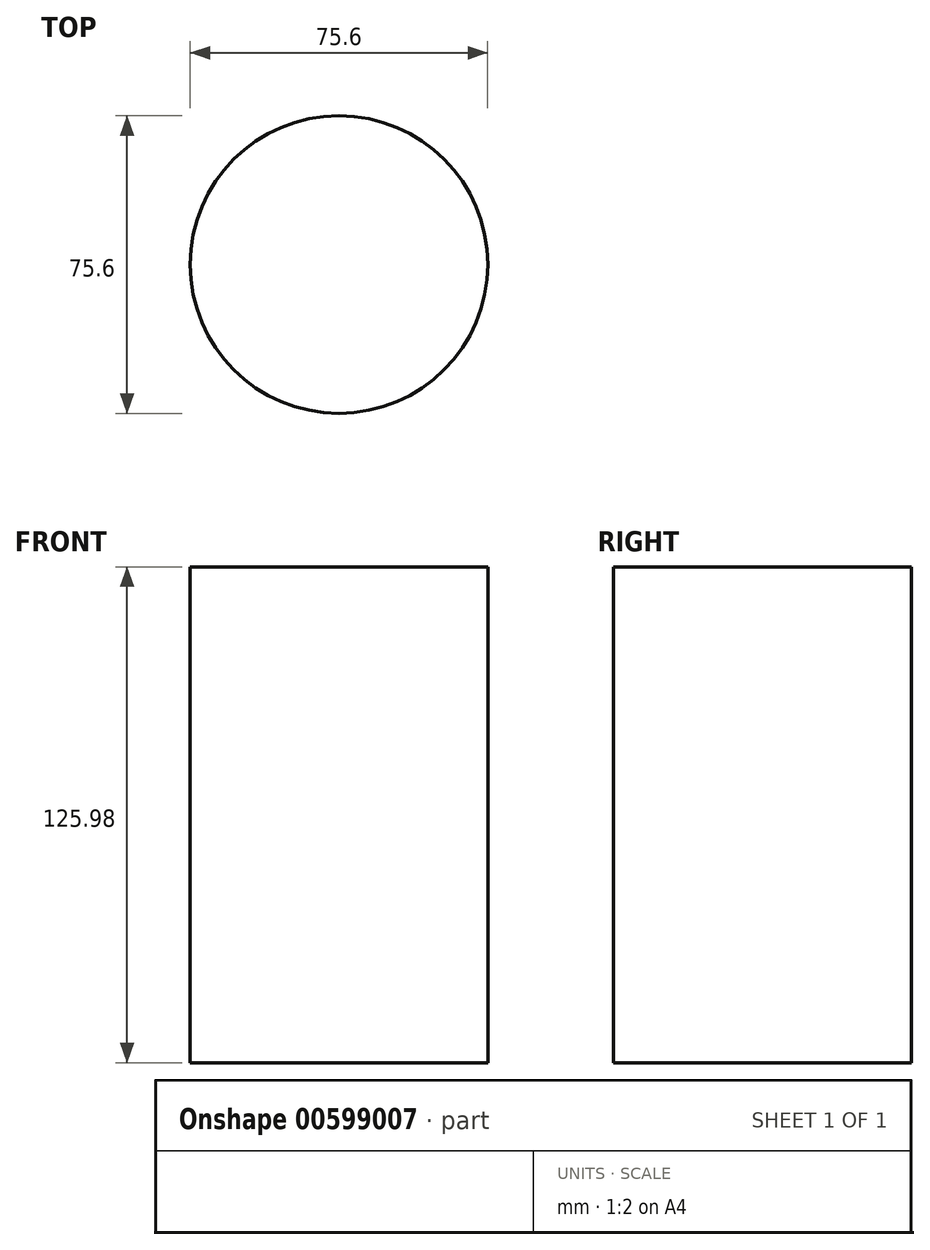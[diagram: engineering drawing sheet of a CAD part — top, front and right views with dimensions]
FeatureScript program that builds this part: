
annotation { "Feature Type Name" : "Feature", "Feature Type Description" : "" }
export const myFeature = defineFeature(function(context is Context, id is Id, definition is map)
    precondition{}
    {
        {
            var Q0;
            Q0=qCreatedBy(makeId("Top.planeOp"),FACE);
            var sketch = newSketch(context, id + "F0", { "sketchPlane" : qUnion([Q0])});
            skCircle(sketch, "E0", {"center": v(-17.9, 8.87) * mm, "radius": 37.8 * mm});
            skSolve(sketch);
        }
        {
            var Q0;
            Q0=makeQuery(id+"F0.imprint","IMPRINT",FACE,{"disambiguationData":[TD([[makeQuery(id+"F0.imprint","IMPRINT",EDGE,{"derivedFrom":sQuery(id+"F0.wireOp",EDGE,"E0")}),1.0]])]});
            extrude(context, id + "F1", {"entities" : qUnion([Q0]), "depth" : 125.98 * mm, "offsetDistance" : 25.4 * mm});
        }
    });
